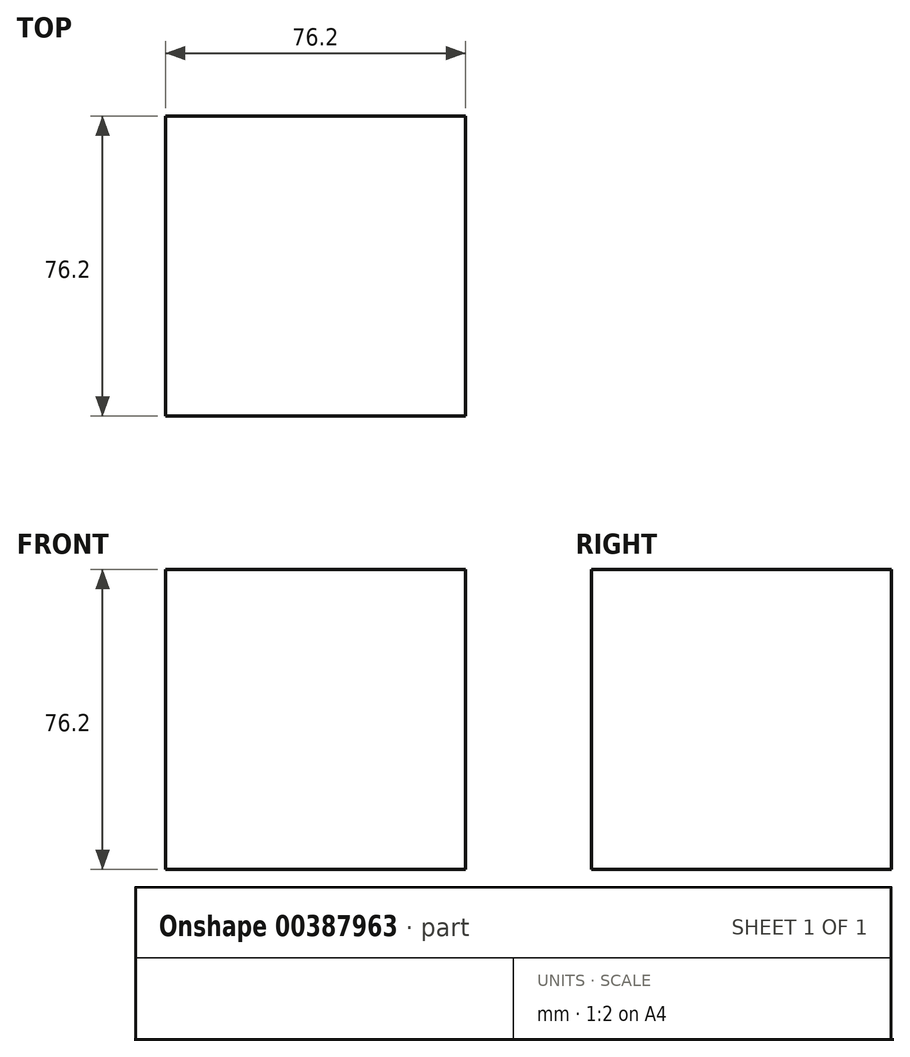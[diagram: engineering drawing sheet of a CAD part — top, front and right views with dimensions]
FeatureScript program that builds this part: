
annotation { "Feature Type Name" : "Feature", "Feature Type Description" : "" }
export const myFeature = defineFeature(function(context is Context, id is Id, definition is map)
    precondition{}
    {
        {
            var Q0;
            Q0=qCreatedBy(makeId("Front.planeOp"),FACE);
            var sketch = newSketch(context, id + "F0", { "sketchPlane" : qUnion([Q0])});
            skLineSegment(sketch, "E0.bottom", {"start": v(-43.99, 41.07) * mm, "end": v(32.21, 41.07) * mm});
            skLineSegment(sketch, "E0.top", {"start": v(-43.99, -35.13) * mm, "end": v(32.21, -35.13) * mm});
            skLineSegment(sketch, "E0.left", {"start": v(-43.99, 41.07) * mm, "end": v(-43.99, -35.13) * mm});
            skLineSegment(sketch, "E0.right", {"start": v(32.21, 41.07) * mm, "end": v(32.21, -35.13) * mm});
            skSolve(sketch);
        }
        {
            var Q0;
            Q0=makeQuery(id+"F0.imprint","IMPRINT",FACE,{"disambiguationData":[TD([[makeQuery(id+"F0.imprint","IMPRINT",EDGE,{"derivedFrom":sQuery(id+"F0.wireOp",EDGE,"E0.bottom")}),-1.0]])]});
            extrude(context, id + "F1", {"entities" : qUnion([Q0]), "depth" : 76.2 * mm});
        }
    });
